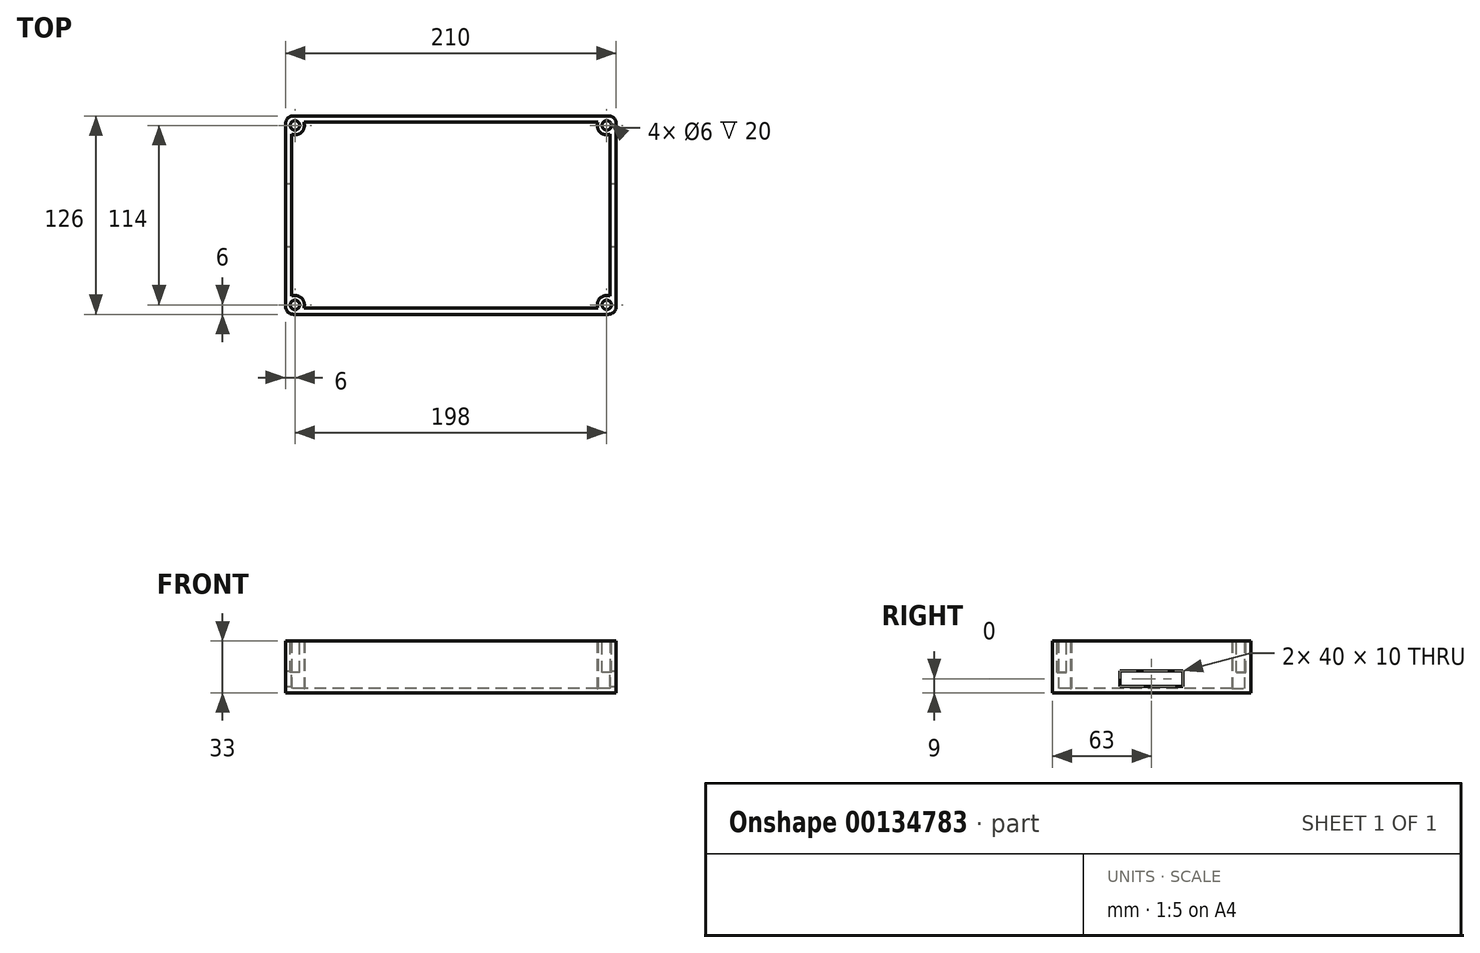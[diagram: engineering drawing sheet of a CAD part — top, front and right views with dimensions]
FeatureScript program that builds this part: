
annotation { "Feature Type Name" : "Feature", "Feature Type Description" : "" }
export const myFeature = defineFeature(function(context is Context, id is Id, definition is map)
    precondition{}
    {
        {
            var Q0;
            Q0=qCreatedBy(makeId("Top.planeOp"),FACE);
            var sketch = newSketch(context, id + "F0", { "sketchPlane" : qUnion([Q0])});
            skLineSegment(sketch, "E0.bottom", {"start": v(105, 63) * mm, "end": v(-105, 63) * mm});
            skLineSegment(sketch, "E0.top", {"start": v(105, -63) * mm, "end": v(-105, -63) * mm});
            skLineSegment(sketch, "E0.left", {"start": v(105, 63) * mm, "end": v(105, -63) * mm});
            skLineSegment(sketch, "E0.right", {"start": v(-105, 63) * mm, "end": v(-105, -63) * mm});
            skPoint(sketch, "E0.middle", {"position": v(0, 0) * mm});
            skCircle(sketch, "E1", {"center": v(-99, 57) * mm, "radius": 6 * mm});
            skCircle(sketch, "E2.0.1.0", {"center": v(-99, -57) * mm, "radius": 6 * mm});
            skCircle(sketch, "E2.1.0.0", {"center": v(99, 57) * mm, "radius": 6 * mm});
            skCircle(sketch, "E2.1.1.0", {"center": v(99, -57) * mm, "radius": 6 * mm});
            skLineSegment(sketch, "E2.direction1", {"start": v(-99, 57) * mm, "end": v(99, 57) * mm, "construction": true});
            skLineSegment(sketch, "E2.direction2", {"start": v(-99, 57) * mm, "end": v(-99, -57) * mm, "construction": true});
            skLineSegment(sketch, "E3.bottom", {"start": v(101, 59) * mm, "end": v(-101, 59) * mm});
            skLineSegment(sketch, "E3.top", {"start": v(101, -59) * mm, "end": v(-101, -59) * mm});
            skLineSegment(sketch, "E3.left", {"start": v(101, 59) * mm, "end": v(101, -59) * mm});
            skLineSegment(sketch, "E3.right", {"start": v(-101, 59) * mm, "end": v(-101, -59) * mm});
            skSolve(sketch);
        }
        {
            var Q0;
            {var subQ0=sQuery(id+"F0.wireOp",EDGE,"E0.left");var subQ1=sQuery(id+"F0.wireOp",EDGE,"E0.bottom");var subQ2=makeQuery(id+"F0.imprint","INTERSECT",VERTEX,{"derivedFrom":[subQ1,subQ0]});Q0=makeQuery(id+"F0.imprint","IMPRINT",FACE,{"disambiguationData":[TD([[makeQuery(id+"F0.imprint","IMPRINT",EDGE,{"disambiguationData":[TD([[subQ2,-1.0]])],"derivedFrom":subQ1}),1.0]])]});}
            var Q1;
            {var subQ0=sQuery(id+"F0.wireOp",EDGE,"E0.right");var subQ1=sQuery(id+"F0.wireOp",EDGE,"E0.bottom");var subQ2=makeQuery(id+"F0.imprint","INTERSECT",VERTEX,{"derivedFrom":[subQ1,subQ0]});Q1=makeQuery(id+"F0.imprint","IMPRINT",FACE,{"disambiguationData":[TD([[makeQuery(id+"F0.imprint","IMPRINT",EDGE,{"disambiguationData":[TD([[subQ2,1.0]])],"derivedFrom":subQ1}),1.0]])]});}
            var Q2;
            {var subQ0=sQuery(id+"F0.wireOp",EDGE,"E0.left");var subQ1=sQuery(id+"F0.wireOp",EDGE,"E0.top");var subQ2=makeQuery(id+"F0.imprint","INTERSECT",VERTEX,{"derivedFrom":[subQ1,subQ0]});Q2=makeQuery(id+"F0.imprint","IMPRINT",FACE,{"disambiguationData":[TD([[makeQuery(id+"F0.imprint","IMPRINT",EDGE,{"disambiguationData":[TD([[subQ2,-1.0]])],"derivedFrom":subQ1}),-1.0]])]});}
            var Q3;
            {var subQ0=sQuery(id+"F0.wireOp",EDGE,"E0.right");var subQ1=sQuery(id+"F0.wireOp",EDGE,"E0.top");var subQ2=makeQuery(id+"F0.imprint","INTERSECT",VERTEX,{"derivedFrom":[subQ1,subQ0]});Q3=makeQuery(id+"F0.imprint","IMPRINT",FACE,{"disambiguationData":[TD([[makeQuery(id+"F0.imprint","IMPRINT",EDGE,{"disambiguationData":[TD([[subQ2,1.0]])],"derivedFrom":subQ1}),-1.0]])]});}
            var Q4;
            {var subQ0=sQuery(id+"F0.wireOp",EDGE,"E2.1.1.0");var subQ1=sQuery(id+"F0.wireOp",EDGE,"E0.top");var subQ2=makeQuery(id+"F0.imprint","INTERSECT",VERTEX,{"derivedFrom":[subQ1,subQ0]});Q4=makeQuery(id+"F0.imprint","IMPRINT",FACE,{"disambiguationData":[TD([[makeQuery(id+"F0.imprint","IMPRINT",EDGE,{"disambiguationData":[TD([[subQ2,-1.0]])],"derivedFrom":subQ1}),-1.0]])]});}
            var Q5;
            {var subQ0=sQuery(id+"F0.wireOp",EDGE,"E2.1.0.0");var subQ1=sQuery(id+"F0.wireOp",EDGE,"E0.left");var subQ2=makeQuery(id+"F0.imprint","INTERSECT",VERTEX,{"derivedFrom":[subQ1,subQ0]});Q5=makeQuery(id+"F0.imprint","IMPRINT",FACE,{"disambiguationData":[TD([[makeQuery(id+"F0.imprint","IMPRINT",EDGE,{"disambiguationData":[TD([[subQ2,-1.0]])],"derivedFrom":subQ1}),-1.0]])]});}
            var Q6;
            {var subQ0=sQuery(id+"F0.wireOp",EDGE,"E1");var subQ1=sQuery(id+"F0.wireOp",EDGE,"E0.right");var subQ2=makeQuery(id+"F0.imprint","INTERSECT",VERTEX,{"derivedFrom":[subQ1,subQ0]});Q6=makeQuery(id+"F0.imprint","IMPRINT",FACE,{"disambiguationData":[TD([[makeQuery(id+"F0.imprint","IMPRINT",EDGE,{"disambiguationData":[TD([[subQ2,-1.0]])],"derivedFrom":subQ1}),1.0]])]});}
            var Q7;
            {var subQ3=sQuery(id+"F0.wireOp",EDGE,"E1");var subQ7=makeQuery(id+"F0.imprint","INTERSECT",VERTEX,{"derivedFrom":[sQuery(id+"F0.wireOp",EDGE,"E0.bottom"),subQ3]});Q7=makeQuery(id+"F0.imprint","IMPRINT",FACE,{"disambiguationData":[TD([[makeQuery(id+"F0.imprint","IMPRINT",EDGE,{"disambiguationData":[TD([[subQ7,1.0]])],"derivedFrom":subQ3}),1.0]])]});}
            var Q8;
            {var subQ3=sQuery(id+"F0.wireOp",EDGE,"E2.0.1.0");var subQ7=makeQuery(id+"F0.imprint","INTERSECT",VERTEX,{"derivedFrom":[sQuery(id+"F0.wireOp",EDGE,"E0.right"),subQ3]});Q8=makeQuery(id+"F0.imprint","IMPRINT",FACE,{"disambiguationData":[TD([[makeQuery(id+"F0.imprint","IMPRINT",EDGE,{"disambiguationData":[TD([[subQ7,1.0]])],"derivedFrom":subQ3}),1.0]])]});}
            var Q9;
            {var subQ3=sQuery(id+"F0.wireOp",EDGE,"E2.1.0.0");var subQ5=makeQuery(id+"F0.imprint","INTERSECT",VERTEX,{"derivedFrom":[sQuery(id+"F0.wireOp",EDGE,"E0.bottom"),subQ3]});Q9=makeQuery(id+"F0.imprint","IMPRINT",FACE,{"disambiguationData":[TD([[makeQuery(id+"F0.imprint","IMPRINT",EDGE,{"disambiguationData":[TD([[subQ5,1.0]])],"derivedFrom":subQ3}),1.0]])]});}
            var Q10;
            {var subQ3=sQuery(id+"F0.wireOp",EDGE,"E2.1.1.0");var subQ5=makeQuery(id+"F0.imprint","INTERSECT",VERTEX,{"derivedFrom":[sQuery(id+"F0.wireOp",EDGE,"E0.left"),subQ3]});Q10=makeQuery(id+"F0.imprint","IMPRINT",FACE,{"disambiguationData":[TD([[makeQuery(id+"F0.imprint","IMPRINT",EDGE,{"disambiguationData":[TD([[subQ5,-1.0]])],"derivedFrom":subQ3}),1.0]])]});}
            var Q11;
            {var subQ0=sQuery(id+"F0.wireOp",EDGE,"E3.bottom");var subQ1=sQuery(id+"F0.wireOp",EDGE,"E2.1.0.0");var subQ2=makeQuery(id+"F0.imprint","INTERSECT",VERTEX,{"derivedFrom":[subQ1,subQ0]});Q11=makeQuery(id+"F0.imprint","IMPRINT",FACE,{"disambiguationData":[TD([[makeQuery(id+"F0.imprint","IMPRINT",EDGE,{"disambiguationData":[TD([[subQ2,-1.0]])],"derivedFrom":subQ1}),1.0]])]});}
            var Q12;
            {var subQ0=sQuery(id+"F0.wireOp",EDGE,"E3.bottom");var subQ1=sQuery(id+"F0.wireOp",EDGE,"E1");var subQ2=makeQuery(id+"F0.imprint","INTERSECT",VERTEX,{"derivedFrom":[subQ1,subQ0]});Q12=makeQuery(id+"F0.imprint","IMPRINT",FACE,{"disambiguationData":[TD([[makeQuery(id+"F0.imprint","IMPRINT",EDGE,{"disambiguationData":[TD([[subQ2,1.0]])],"derivedFrom":subQ1}),1.0]])]});}
            var Q13;
            {var subQ0=sQuery(id+"F0.wireOp",EDGE,"E3.right");var subQ1=sQuery(id+"F0.wireOp",EDGE,"E2.0.1.0");var subQ2=makeQuery(id+"F0.imprint","INTERSECT",VERTEX,{"derivedFrom":[subQ1,subQ0]});Q13=makeQuery(id+"F0.imprint","IMPRINT",FACE,{"disambiguationData":[TD([[makeQuery(id+"F0.imprint","IMPRINT",EDGE,{"disambiguationData":[TD([[subQ2,1.0]])],"derivedFrom":subQ1}),1.0]])]});}
            var Q14;
            {var subQ0=sQuery(id+"F0.wireOp",EDGE,"E3.left");var subQ1=sQuery(id+"F0.wireOp",EDGE,"E2.1.1.0");var subQ2=makeQuery(id+"F0.imprint","INTERSECT",VERTEX,{"derivedFrom":[subQ1,subQ0]});Q14=makeQuery(id+"F0.imprint","IMPRINT",FACE,{"disambiguationData":[TD([[makeQuery(id+"F0.imprint","IMPRINT",EDGE,{"disambiguationData":[TD([[subQ2,-1.0]])],"derivedFrom":subQ1}),1.0]])]});}
            var Q15;
            {var subQ0=sQuery(id+"F0.wireOp",EDGE,"E2.1.0.0");var subQ1=sQuery(id+"F0.wireOp",EDGE,"E0.bottom");var subQ2=makeQuery(id+"F0.imprint","INTERSECT",VERTEX,{"derivedFrom":[subQ1,subQ0]});Q15=makeQuery(id+"F0.imprint","IMPRINT",FACE,{"disambiguationData":[TD([[makeQuery(id+"F0.imprint","IMPRINT",EDGE,{"disambiguationData":[TD([[subQ2,-1.0]])],"derivedFrom":subQ1}),1.0]])]});}
            extrude(context, id + "F1", {"entities" : qUnion([Q0, Q1, Q2, Q3, Q4, Q5, Q6, Q7, Q8, Q9, Q10, Q11, Q12, Q13, Q14, Q15]), "depth" : 33 * mm});
        }
        {
            var Q0;
            Q0=qCreatedBy(makeId("Top.planeOp"),FACE);
            var sketch = newSketch(context, id + "F2", { "sketchPlane" : qUnion([Q0])});
            skLineSegment(sketch, "E4.bottom", {"start": v(105, -63) * mm, "end": v(-105, -63) * mm});
            skLineSegment(sketch, "E4.top", {"start": v(105, 63) * mm, "end": v(-105, 63) * mm});
            skLineSegment(sketch, "E4.left", {"start": v(105, -63) * mm, "end": v(105, 63) * mm});
            skLineSegment(sketch, "E4.right", {"start": v(-105, -63) * mm, "end": v(-105, 63) * mm});
            skPoint(sketch, "E4.middle", {"position": v(0, 0) * mm});
            skSolve(sketch);
        }
        {
            var Q0;
            Q0=makeQuery(id+"F2.imprint","IMPRINT",FACE,{"disambiguationData":[TD([[makeQuery(id+"F2.imprint","IMPRINT",EDGE,{"derivedFrom":sQuery(id+"F2.wireOp",EDGE,"E4.bottom")}),-1.0]])]});
            extrude(context, id + "F3", {"entities" : qUnion([Q0]), "operationType" : NewBodyOperationType.ADD, "depth" : 3 * mm});
        }
        {
            var Q0;
            Q0=makeQuery(id+"F1.opExtrude","SWEPT_FACE",FACE,{"disambiguationData":[OSD([sQuery(id+"F0.wireOp",EDGE,"E0.left")])]});
            var sketch = newSketch(context, id + "F4", { "sketchPlane" : qUnion([Q0])});
            skLineSegment(sketch, "E5.bottom", {"start": v(20, 4) * mm, "end": v(-20, 4) * mm});
            skLineSegment(sketch, "E5.top", {"start": v(20, 14) * mm, "end": v(-20, 14) * mm});
            skLineSegment(sketch, "E5.left", {"start": v(20, 4) * mm, "end": v(20, 14) * mm});
            skLineSegment(sketch, "E5.right", {"start": v(-20, 4) * mm, "end": v(-20, 14) * mm});
            skPoint(sketch, "E5.middle", {"position": v(0, 9) * mm});
            skSolve(sketch);
        }
        {
            var Q0;
            Q0=makeQuery(id+"F4.imprint","IMPRINT",FACE,{"disambiguationData":[TD([[makeQuery(id+"F4.imprint","IMPRINT",EDGE,{"derivedFrom":sQuery(id+"F4.wireOp",EDGE,"E5.bottom")}),-1.0]])]});
            extrude(context, id + "F5", {"entities" : qUnion([Q0]), "operationType" : NewBodyOperationType.REMOVE, "endBound" : BoundingType.THROUGH_ALL, "oppositeDirection" : true, "depth" : 25 * mm});
        }
        {
            var Q0;
            Q0=makeQuery(id+"F1.opExtrude","SWEPT_EDGE",EDGE,{"disambiguationData":[OSD([sQuery(id+"F0.wireOp",EDGE,"E0.bottom"),sQuery(id+"F0.wireOp",EDGE,"E0.right")])]});
            var Q1;
            Q1=makeQuery(id+"F1.opExtrude","SWEPT_EDGE",EDGE,{"disambiguationData":[OSD([sQuery(id+"F0.wireOp",EDGE,"E0.bottom"),sQuery(id+"F0.wireOp",EDGE,"E0.left")])]});
            var Q2;
            Q2=makeQuery(id+"F1.opExtrude","SWEPT_EDGE",EDGE,{"disambiguationData":[OSD([sQuery(id+"F0.wireOp",EDGE,"E0.top"),sQuery(id+"F0.wireOp",EDGE,"E0.left")])]});
            var Q3;
            Q3=makeQuery(id+"F1.opExtrude","SWEPT_EDGE",EDGE,{"disambiguationData":[OSD([sQuery(id+"F0.wireOp",EDGE,"E0.top"),sQuery(id+"F0.wireOp",EDGE,"E0.right")])]});
            fillet(context, id + "F6", {"entities" : qUnion([Q0, Q1, Q2, Q3]), "radius" : 5 * mm, "tangentPropagation" : true, "allowEdgeOverflow" : false});
        }
        {
            var Q0;
            Q0=makeQuery(id+"F1.opExtrude","CAP_FACE",FACE,{"disambiguationData":[OSD([sQuery(id+"F0.wireOp",EDGE,"E0.bottom"),sQuery(id+"F0.wireOp",EDGE,"E0.top"),sQuery(id+"F0.wireOp",EDGE,"E0.left"),sQuery(id+"F0.wireOp",EDGE,"E0.right"),sQuery(id+"F0.wireOp",EDGE,"E1"),sQuery(id+"F0.wireOp",EDGE,"E2.0.1.0"),sQuery(id+"F0.wireOp",EDGE,"E2.1.0.0"),sQuery(id+"F0.wireOp",EDGE,"E2.1.1.0"),sQuery(id+"F0.wireOp",EDGE,"E3.bottom"),sQuery(id+"F0.wireOp",EDGE,"E3.top"),sQuery(id+"F0.wireOp",EDGE,"E3.left"),sQuery(id+"F0.wireOp",EDGE,"E3.right")])],"isStart":false});
            var sketch = newSketch(context, id + "F7", { "sketchPlane" : qUnion([Q0])});
            skCircle(sketch, "E6", {"center": v(-99, 57) * mm, "radius": 3 * mm});
            skCircle(sketch, "E7", {"center": v(99, 57) * mm, "radius": 3 * mm});
            skCircle(sketch, "E8", {"center": v(99, -57) * mm, "radius": 3 * mm});
            skCircle(sketch, "E9", {"center": v(-99, -57) * mm, "radius": 3 * mm});
            skSolve(sketch);
        }
        {
            var Q0;
            Q0=makeQuery(id+"F7.imprint","IMPRINT",FACE,{"disambiguationData":[TD([[makeQuery(id+"F7.imprint","IMPRINT",EDGE,{"derivedFrom":sQuery(id+"F7.wireOp",EDGE,"E6")}),1.0]])]});
            var Q1;
            Q1=makeQuery(id+"F7.imprint","IMPRINT",FACE,{"disambiguationData":[TD([[makeQuery(id+"F7.imprint","IMPRINT",EDGE,{"derivedFrom":sQuery(id+"F7.wireOp",EDGE,"E7")}),1.0]])]});
            var Q2;
            Q2=makeQuery(id+"F7.imprint","IMPRINT",FACE,{"disambiguationData":[TD([[makeQuery(id+"F7.imprint","IMPRINT",EDGE,{"derivedFrom":sQuery(id+"F7.wireOp",EDGE,"E8")}),1.0]])]});
            var Q3;
            Q3=makeQuery(id+"F7.imprint","IMPRINT",FACE,{"disambiguationData":[TD([[makeQuery(id+"F7.imprint","IMPRINT",EDGE,{"derivedFrom":sQuery(id+"F7.wireOp",EDGE,"E9")}),1.0]])]});
            extrude(context, id + "F8", {"entities" : qUnion([Q0, Q1, Q2, Q3]), "operationType" : NewBodyOperationType.REMOVE, "oppositeDirection" : true, "depth" : 20 * mm});
        }
    });
